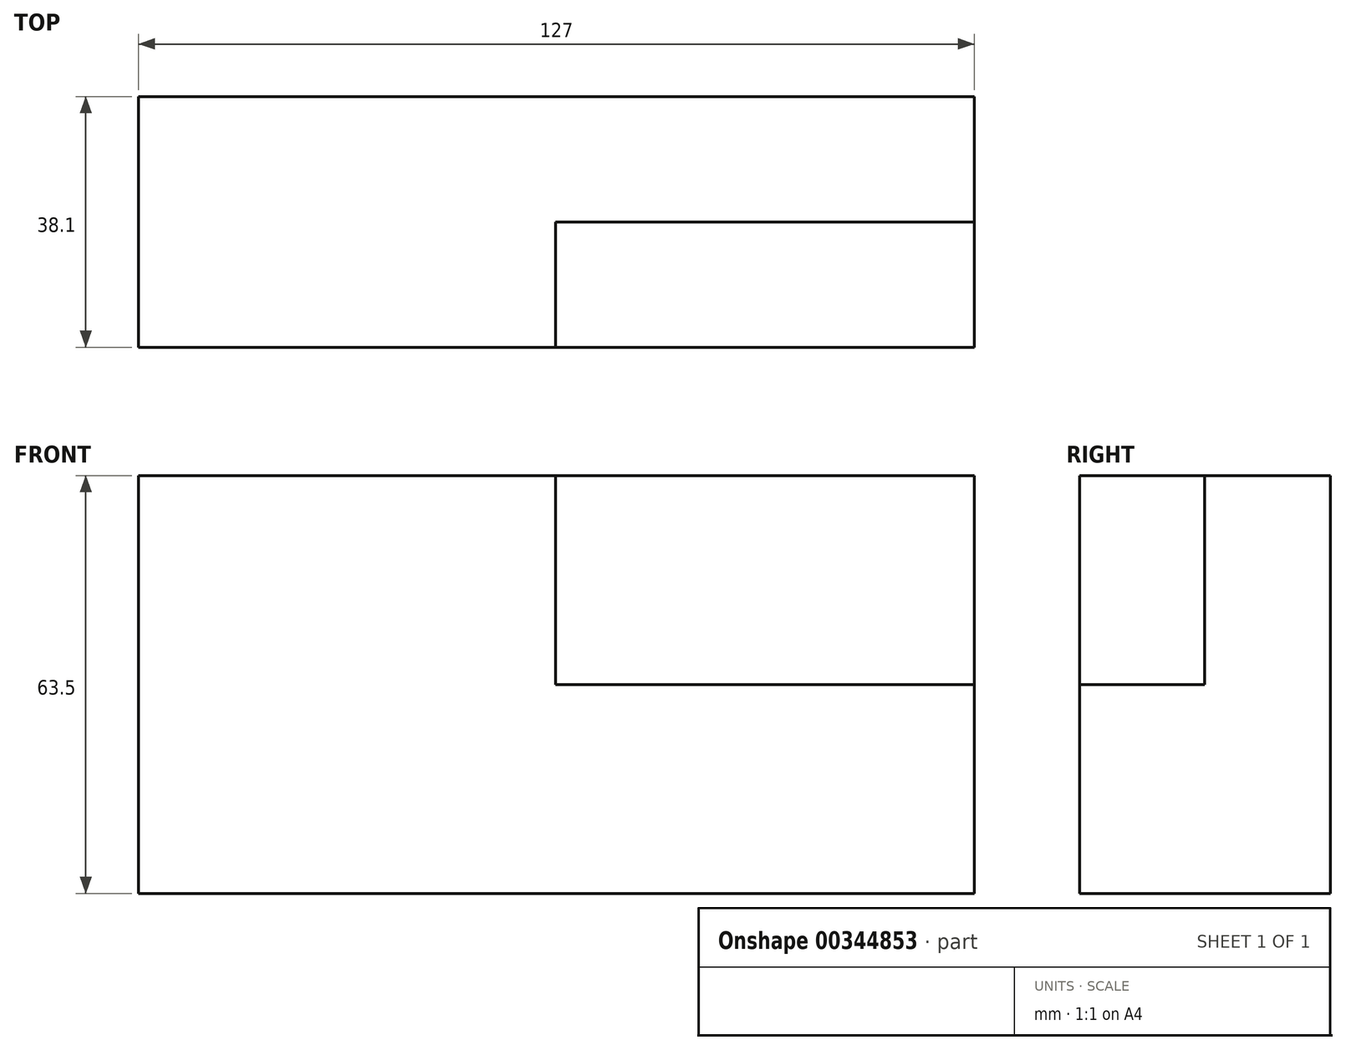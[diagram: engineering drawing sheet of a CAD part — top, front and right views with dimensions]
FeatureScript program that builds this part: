
annotation { "Feature Type Name" : "Feature", "Feature Type Description" : "" }
export const myFeature = defineFeature(function(context is Context, id is Id, definition is map)
    precondition{}
    {
        {
            var Q0;
            Q0=qCreatedBy(makeId("Front.planeOp"),FACE);
            var sketch = newSketch(context, id + "F0", { "sketchPlane" : qUnion([Q0])});
            skLineSegment(sketch, "E0.bottom", {"start": v(63.5, 31.75) * mm, "end": v(-63.5, 31.75) * mm});
            skLineSegment(sketch, "E0.top", {"start": v(63.5, -31.75) * mm, "end": v(-63.5, -31.75) * mm});
            skLineSegment(sketch, "E0.left", {"start": v(63.5, 31.75) * mm, "end": v(63.5, -31.75) * mm});
            skLineSegment(sketch, "E0.right", {"start": v(-63.5, 31.75) * mm, "end": v(-63.5, -31.75) * mm});
            skPoint(sketch, "E0.middle", {"position": v(0, 0) * mm});
            skSolve(sketch);
        }
        {
            var Q0;
            Q0 = qSketchRegion(id + "F0", true);
            extrude(context, id + "F1", {"entities" : qUnion([Q0]), "depth" : 38.1 * mm});
        }
        {
            var Q0;
            Q0=qCreatedBy(makeId("Top.planeOp"),FACE);
            var sketch = newSketch(context, id + "F2", { "sketchPlane" : qUnion([Q0])});
            skLineSegment(sketch, "E1.right", {"start": v(-0.13, -35.55) * mm, "end": v(-0.13, -19.1) * mm});
            skLineSegment(sketch, "E2.bottom", {"start": v(63.37, -38.14) * mm, "end": v(-0.13, -38.14) * mm});
            skLineSegment(sketch, "E2.top", {"start": v(63.37, -19.1) * mm, "end": v(-0.13, -19.1) * mm});
            skLineSegment(sketch, "E2.right", {"start": v(-0.13, -38.14) * mm, "end": v(-0.13, -19.1) * mm});
            skLineSegment(sketch, "E3", {"start": v(63.37, -19.1) * mm, "end": v(74.7, -19.1) * mm});
            skLineSegment(sketch, "E4", {"start": v(74.7, -19.1) * mm, "end": v(74.7, -38.14) * mm});
            skLineSegment(sketch, "E5", {"start": v(74.7, -38.14) * mm, "end": v(63.37, -38.14) * mm});
            skSolve(sketch);
        }
        {
            var Q0;
            Q0 = qSketchRegion(id + "F2", true);
            extrude(context, id + "F3", {"entities" : qUnion([Q0]), "operationType" : NewBodyOperationType.REMOVE, "depth" : 60.96 * mm});
        }
    });
